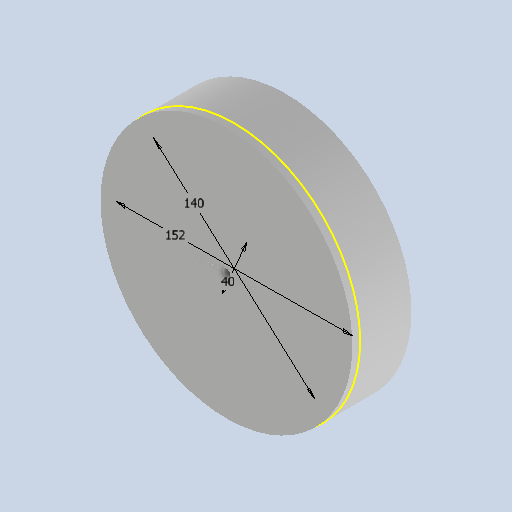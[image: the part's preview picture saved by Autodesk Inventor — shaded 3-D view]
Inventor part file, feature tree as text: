
AUTODESK INVENTOR PART (.ipt)
format: ipt  version: 2025 (Build 290162010, 162A)  size: 209,408 bytes
history: native  units: mm
features: reference x6, extrude x3, sketch x3, hole x3, other x3, projected_geometry x1
ambient origin geometry x8: Origin, YZ Plane, XZ Plane, XY Plane, X Axis, Y Axis, Z Axis, Center Point
bodies: Volumenkörper1 (feature_tree)
feature tree (19):
  extrude  "Extrusion1"  Depth=5.0mm TaperAngle=0.0deg
  sketch  "Skizze2"  dims[d3=140.0mm d4=40.0mm]
  hole  "Bohrung1"  [1 undecoded]
  extrude  "Extrusion2"  Depth=2.5mm TaperAngle=0.0deg
  hole  "Bohrung2"  [1 undecoded]
  extrude  "Extrusion3"  Depth=33.0mm TaperAngle=0.0deg
  hole  "Bohrung3"  [1 undecoded]
  sketch  "Skizze1"  dims[d0=162.0mm d1=5.0mm d2=0.0mm]
  projected_geometry  "Projizierte Kontur1"
  sketch  "Skizze3"  dims[d5=5.0mm d6=6.0mm d7=4.0mm d8=2.0mm d9=90.0deg d10=8.0mm d11=20.594885mm d12=2.5mm d13=0.0mm d14=0.7mm d15=6.0mm d16=4.0mm d17=2.0mm d18=90.0deg d19=8.0mm d20=20.594885mm d21=152.0mm d22=33.0mm d23=0.0mm d24=0.929367mm d25=2.4mm d26=4.4mm d27=2.0mm d28=90.0deg d29=10.0mm d30=20.594885mm]
  reference  "Referenz1"
  reference  "Referenz2"
  reference  "Referenz3"
  reference  "Referenz4"
  reference  "Referenz5"
  reference  "Referenz6"
  other  "<userpath>\GIT\pillbox\Baugruppe1.iam"
  other  "Baugruppe1.iam"
  other  "Bauteil3:1"
note: 3 required parameter values undecoded (feature->parameter linkage not recoverable at this tier; creation-order binding heuristic only, values carry confidence <= 0.55)
